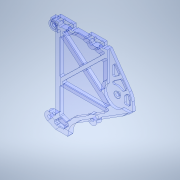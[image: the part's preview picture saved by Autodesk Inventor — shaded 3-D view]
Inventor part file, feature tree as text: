
AUTODESK INVENTOR PART (.ipt)
format: ipt  version: 2020.2 (Build 242310000, 310)  size: 1,229,824 bytes
history: native  units: mm
features: extrude x21, sketch x18, projected_geometry x14, hole x3, other x2, fillet x2
ambient origin geometry x8: Origin, YZ Plane, XZ Plane, XY Plane, X Axis, Y Axis, Z Axis, Center Point
bodies: Body1 (feature_tree)
feature tree (60):
  other  "ソリッド1"
  sketch  "スケッチ1"
  extrude  "押し出し1"  Depth=5.0mm
  extrude  "押し出し2"  Depth=3.0mm
  extrude  "押し出し3"  Depth=5.0mm
  extrude  "押し出し4"  Depth=3.0mm
  sketch  "スケッチ4"
  sketch  "スケッチ6"
  sketch  "スケッチ8"
  extrude  "押し出し10"  Depth=3.0mm
  extrude  "押し出し11"  Depth=5.0mm
  extrude  "押し出し12"  Depth=1.0mm
  extrude  "押し出し13"  Depth=5.0mm
  extrude  "押し出し14"  Depth=5.0mm
  sketch  "スケッチ9"
  extrude  "押し出し15"  Depth=2.0mm
  extrude  "押し出し16"  Depth=2.0mm
  extrude  "押し出し17"  Depth=2.0mm
  sketch  "スケッチ11"
  extrude  "押し出し18"  Depth=2.0mm
  extrude  "押し出し19"  Depth=2.0mm
  hole  "穴1"  [1 undecoded]
  sketch  "スケッチ12"
  sketch  "スケッチ13"
  extrude  "押し出し20"  Depth=2.0mm
  extrude  "押し出し21"  Depth=2.0mm
  hole  "穴2"  [1 undecoded]
  sketch  "スケッチ14"
  extrude  "押し出し22"  Depth=2.0mm
  sketch  "スケッチ16"
  extrude  "押し出し23"  Depth=2.0mm
  hole  "穴3"  [1 undecoded]
  fillet  "フィレット1"  Radius=5.0mm
  extrude  "押し出し24"  Depth=2.55mm TaperAngle=0.0deg
  fillet  "フィレット2"  Radius=6.0mm
  sketch  "スケッチ18"
  extrude  "押し出し25"  Depth=3.0mm TaperAngle=0.0deg
  extrude  "押し出し26"  Depth=2.0mm TaperAngle=0.0deg
  sketch  "スケッチ2"
  projected_geometry  "投影ループ1"
  sketch  "スケッチ3"
  projected_geometry  "投影ループ2"
  projected_geometry  "投影ループ3"
  projected_geometry  "投影ループ5"
  projected_geometry  "投影ループ6"
  projected_geometry  "投影ループ9"
  sketch  "スケッチ10"
  projected_geometry  "投影ループ10"
  projected_geometry  "投影ループ11"
  projected_geometry  "投影ループ12"
  projected_geometry  "投影ループ13"
  projected_geometry  "投影ループ14"
  sketch  "スケッチ15"
  sketch  "スケッチ17"
  projected_geometry  "投影ループ15"
  projected_geometry  "投影ループ16"
  projected_geometry  "投影ループ17"
  sketch  "スケッチ19"
  sketch  "スケッチ20"
  other  "断面エッジを投影1"
note: 3 required parameter values undecoded (feature->parameter linkage not recoverable at this tier; creation-order binding heuristic only, values carry confidence <= 0.55)
